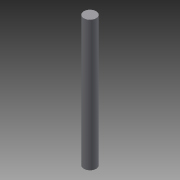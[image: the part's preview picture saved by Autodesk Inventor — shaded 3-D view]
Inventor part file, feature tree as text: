
AUTODESK INVENTOR PART (.ipt)
format: ipt  version: 2014 SP1 (Build 180222100, 222)  size: 63,488 bytes
history: native  units: in
note: dims shown in document units (in); Inventor stores cm internally (conversion verified against a paired STEP export)
features: extrude x1, sketch x1
ambient origin geometry x8: Origin, YZ Plane, XZ Plane, XY Plane, X Axis, Y Axis, Z Axis, Center Point
bodies: Solid1 (feature_tree)
feature tree (2):
  extrude  "Extrusion1"  Depth=2.0in TaperAngle=0.0deg
  sketch  "Sketch1"  dims[d0=0.19in d1=2.0in d2=0.0in]
